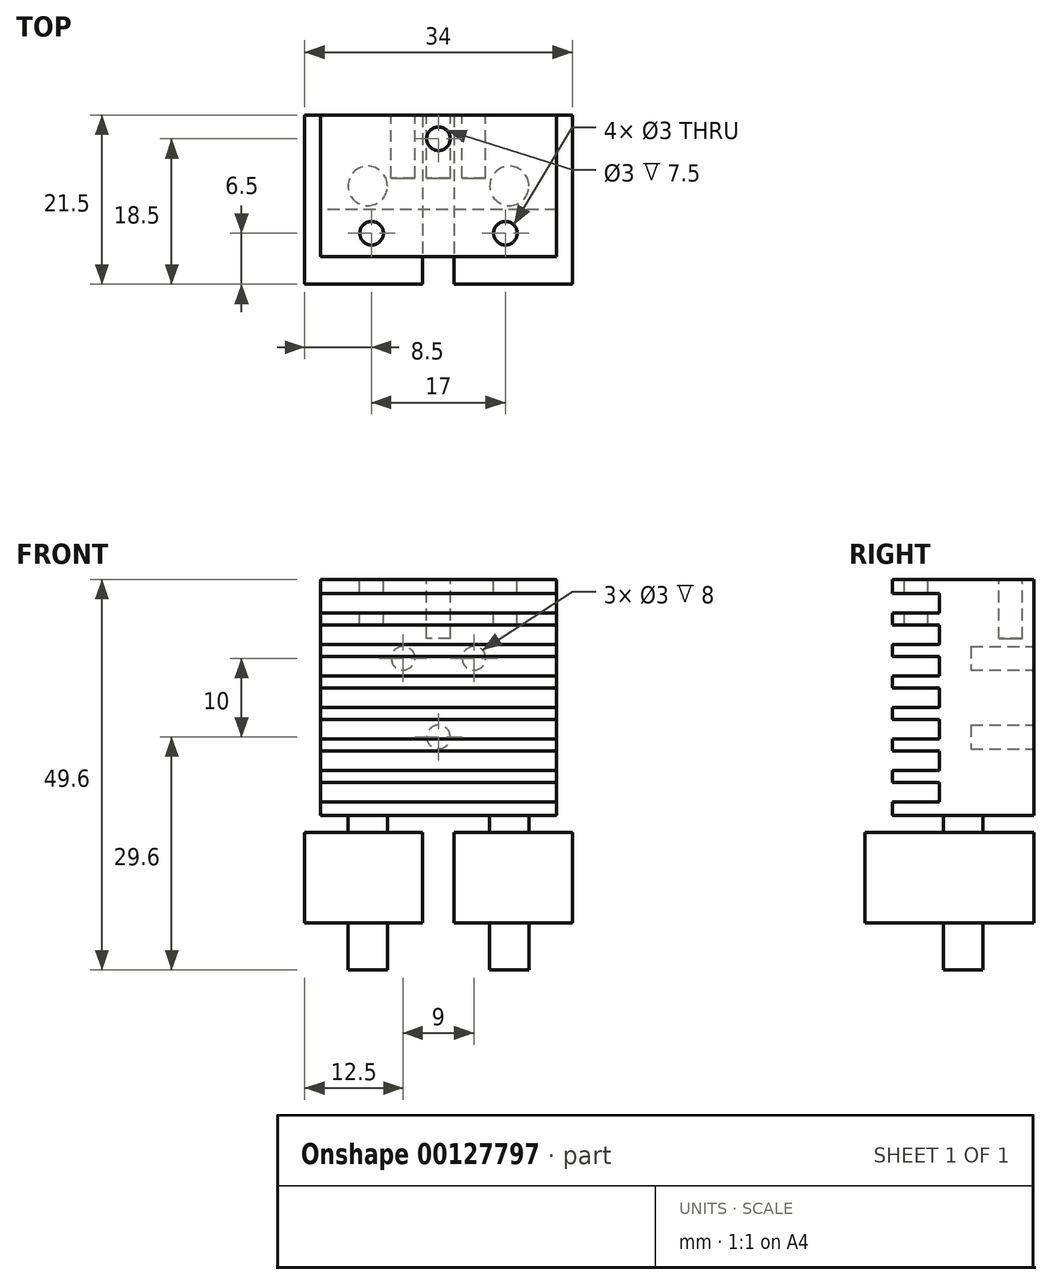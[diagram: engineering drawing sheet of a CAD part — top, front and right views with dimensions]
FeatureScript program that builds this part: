
annotation { "Feature Type Name" : "Feature", "Feature Type Description" : "" }
export const myFeature = defineFeature(function(context is Context, id is Id, definition is map)
    precondition{}
    {
        {
            var Q0;
            Q0=qCreatedBy(makeId("Front.planeOp"),FACE);
            var sketch = newSketch(context, id + "F0", { "sketchPlane" : qUnion([Q0])});
            skLineSegment(sketch, "E0.bottom", {"start": v(15, 15) * mm, "end": v(-15, 15) * mm});
            skLineSegment(sketch, "E0.top", {"start": v(15, -15) * mm, "end": v(-15, -15) * mm});
            skLineSegment(sketch, "E0.left", {"start": v(15, 15) * mm, "end": v(15, -15) * mm});
            skLineSegment(sketch, "E0.right", {"start": v(-15, 15) * mm, "end": v(-15, -15) * mm});
            skPoint(sketch, "E0.middle", {"position": v(0, 0) * mm});
            skSolve(sketch);
        }
        {
            var Q0;
            Q0 = qSketchRegion(id + "F0", true);
            extrude(context, id + "F1", {"entities" : qUnion([Q0]), "endBound" : BoundingType.SYMMETRIC, "depth" : 18 * mm});
        }
        {
            var Q0;
            Q0=makeQuery(id+"F1.opExtrude","SWEPT_FACE",FACE,{"disambiguationData":[OSD([sQuery(id+"F0.wireOp",EDGE,"E0.top")])]});
            var sketch = newSketch(context, id + "F2", { "sketchPlane" : qUnion([Q0])});
            skCircle(sketch, "E1", {"center": v(-9, 0) * mm, "radius": 2.5 * mm});
            skLineSegment(sketch, "E2", {"start": v(0, 0) * mm, "end": v(0, 26.39) * mm, "construction": true});
            skPoint(sketch, "E2.endSnap0", {"position": v(0, 9) * mm});
            skCircle(sketch, "E3.MirrorC", {"center": v(9, 0) * mm, "radius": 2.5 * mm});
            skSolve(sketch);
        }
        {
            var Q0;
            Q0 = qSketchRegion(id + "F2", true);
            extrude(context, id + "F3", {"entities" : qUnion([Q0]), "operationType" : NewBodyOperationType.ADD, "depth" : (49.6 - 30) * mm});
        }
        {
            var Q0;
            Q0=makeQuery(id+"F1.opExtrude","SWEPT_FACE",FACE,{"disambiguationData":[OSD([sQuery(id+"F0.wireOp",EDGE,"E0.right")])]});
            var sketch = newSketch(context, id + "F4", { "sketchPlane" : qUnion([Q0])});
            skLineSegment(sketch, "E4.bottom", {"start": v(9, 13.25) * mm, "end": v(3, 13.25) * mm});
            skLineSegment(sketch, "E4.top", {"start": v(9, 10.75) * mm, "end": v(3, 10.75) * mm});
            skLineSegment(sketch, "E4.left", {"start": v(9, 13.25) * mm, "end": v(9, 10.75) * mm});
            skLineSegment(sketch, "E4.right", {"start": v(3, 13.25) * mm, "end": v(3, 10.75) * mm});
            skLineSegment(sketch, "E5.1.0.0", {"start": v(3, 9.25) * mm, "end": v(3, 6.75) * mm});
            skLineSegment(sketch, "E5.1.0.1", {"start": v(9, 9.25) * mm, "end": v(9, 6.75) * mm});
            skLineSegment(sketch, "E5.1.0.2", {"start": v(9, 6.75) * mm, "end": v(3, 6.75) * mm});
            skLineSegment(sketch, "E5.1.0.3", {"start": v(9, 9.25) * mm, "end": v(3, 9.25) * mm});
            skLineSegment(sketch, "E5.2.0.0", {"start": v(3, 5.25) * mm, "end": v(3, 2.75) * mm});
            skLineSegment(sketch, "E5.2.0.1", {"start": v(9, 5.25) * mm, "end": v(9, 2.75) * mm});
            skLineSegment(sketch, "E5.2.0.2", {"start": v(9, 2.75) * mm, "end": v(3, 2.75) * mm});
            skLineSegment(sketch, "E5.2.0.3", {"start": v(9, 5.25) * mm, "end": v(3, 5.25) * mm});
            skLineSegment(sketch, "E5.direction1", {"start": v(3, 10.75) * mm, "end": v(3, 6.75) * mm, "construction": true});
            skLineSegment(sketch, "E6.0.3.0", {"start": v(3, 1.25) * mm, "end": v(3, -1.25) * mm});
            skLineSegment(sketch, "E6.3.3.0", {"start": v(9, 1.25) * mm, "end": v(9, -1.25) * mm});
            skLineSegment(sketch, "E6.6.3.0", {"start": v(9, -1.25) * mm, "end": v(3, -1.25) * mm});
            skLineSegment(sketch, "E6.9.3.0", {"start": v(9, 1.25) * mm, "end": v(3, 1.25) * mm});
            skLineSegment(sketch, "E6.0.4.0", {"start": v(3, -2.75) * mm, "end": v(3, -5.25) * mm});
            skLineSegment(sketch, "E6.3.4.0", {"start": v(9, -2.75) * mm, "end": v(9, -5.25) * mm});
            skLineSegment(sketch, "E6.6.4.0", {"start": v(9, -5.25) * mm, "end": v(3, -5.25) * mm});
            skLineSegment(sketch, "E6.9.4.0", {"start": v(9, -2.75) * mm, "end": v(3, -2.75) * mm});
            skLineSegment(sketch, "E7.0.5.0", {"start": v(3, -6.75) * mm, "end": v(3, -9.25) * mm});
            skLineSegment(sketch, "E7.3.5.0", {"start": v(9, -6.75) * mm, "end": v(9, -9.25) * mm});
            skLineSegment(sketch, "E7.6.5.0", {"start": v(9, -9.25) * mm, "end": v(3, -9.25) * mm});
            skLineSegment(sketch, "E7.9.5.0", {"start": v(9, -6.75) * mm, "end": v(3, -6.75) * mm});
            skLineSegment(sketch, "E8.0.6.0", {"start": v(3, -10.75) * mm, "end": v(3, -13.25) * mm});
            skLineSegment(sketch, "E8.3.6.0", {"start": v(9, -10.75) * mm, "end": v(9, -13.25) * mm});
            skLineSegment(sketch, "E8.6.6.0", {"start": v(9, -13.25) * mm, "end": v(3, -13.25) * mm});
            skLineSegment(sketch, "E8.9.6.0", {"start": v(9, -10.75) * mm, "end": v(3, -10.75) * mm});
            skSolve(sketch);
        }
        {
            var Q0;
            Q0 = qSketchRegion(id + "F4", true);
            extrude(context, id + "F5", {"entities" : qUnion([Q0]), "operationType" : NewBodyOperationType.REMOVE, "endBound" : BoundingType.THROUGH_ALL, "oppositeDirection" : true, "depth" : 25 * mm});
        }
        {
            var Q0;
            Q0=makeQuery(id+"F1.opExtrude","CAP_FACE",FACE,{"disambiguationData":[OSD([sQuery(id+"F0.wireOp",EDGE,"E0.bottom"),sQuery(id+"F0.wireOp",EDGE,"E0.top"),sQuery(id+"F0.wireOp",EDGE,"E0.left"),sQuery(id+"F0.wireOp",EDGE,"E0.right")])],"isStart":true});
            var sketch = newSketch(context, id + "F6", { "sketchPlane" : qUnion([Q0])});
            skCircle(sketch, "E9", {"center": v(0, -5) * mm, "radius": 1.5 * mm});
            skCircle(sketch, "E10", {"center": v(-4.5, 5) * mm, "radius": 1.5 * mm});
            skCircle(sketch, "E11", {"center": v(4.5, 5) * mm, "radius": 1.5 * mm});
            skLineSegment(sketch, "E12", {"start": v(0, 0) * mm, "end": v(0, 11.94) * mm, "construction": true});
            skSolve(sketch);
        }
        {
            var Q0;
            Q0 = qSketchRegion(id + "F6", true);
            extrude(context, id + "F7", {"entities" : qUnion([Q0]), "operationType" : NewBodyOperationType.REMOVE, "oppositeDirection" : true, "depth" : 8 * mm});
        }
        {
            var Q0;
            Q0=makeQuery(id+"F1.opExtrude","SWEPT_FACE",FACE,{"disambiguationData":[OSD([sQuery(id+"F0.wireOp",EDGE,"E0.bottom")])]});
            var sketch = newSketch(context, id + "F8", { "sketchPlane" : qUnion([Q0])});
            skCircle(sketch, "E13", {"center": v(0, 6) * mm, "radius": 1.5 * mm});
            skCircle(sketch, "E14", {"center": v(8.5, -6) * mm, "radius": 1.5 * mm});
            skCircle(sketch, "E15", {"center": v(-8.5, -6) * mm, "radius": 1.5 * mm});
            skLineSegment(sketch, "E16", {"start": v(0, 0) * mm, "end": v(0, -17.41) * mm, "construction": true});
            skSolve(sketch);
        }
        {
            var Q0;
            Q0 = qSketchRegion(id + "F8", true);
            extrude(context, id + "F9", {"entities" : qUnion([Q0]), "operationType" : NewBodyOperationType.REMOVE, "oppositeDirection" : true, "depth" : 7.5 * mm});
        }
        {
            var Q0;
            Q0=makeQuery(id+"F1.opExtrude","SWEPT_FACE",FACE,{"disambiguationData":[OSD([sQuery(id+"F0.wireOp",EDGE,"E0.top")])]});
            cPlane(context, id + "F10", {"entities" : qUnion([Q0]), "cplaneType" : CPlaneType.OFFSET, "offset" : 2.1 * mm, "width" : 150 * mm, "height" : 150 * mm});
        }
        {
            var Q0;
            Q0=qCreatedBy(id+"F10.planeOp",FACE);
            var sketch = newSketch(context, id + "F11", { "sketchPlane" : qUnion([Q0])});
            skLineSegment(sketch, "E17.bottom", {"start": v(-17, -9) * mm, "end": v(-2, -9) * mm});
            skLineSegment(sketch, "E17.top", {"start": v(-17, 12.5) * mm, "end": v(-2, 12.5) * mm});
            skLineSegment(sketch, "E17.left", {"start": v(-17, -9) * mm, "end": v(-17, 12.5) * mm});
            skLineSegment(sketch, "E17.right", {"start": v(-2, -9) * mm, "end": v(-2, 12.5) * mm});
            skLineSegment(sketch, "E18", {"start": v(0, 0) * mm, "end": v(0, -21.53) * mm, "construction": true});
            skLineSegment(sketch, "E19.MirrorCS", {"start": v(2, -9) * mm, "end": v(2, 12.5) * mm});
            skLineSegment(sketch, "E20.MirrorCS", {"start": v(17, -9) * mm, "end": v(17, 12.5) * mm});
            skLineSegment(sketch, "E21.MirrorCS", {"start": v(17, -9) * mm, "end": v(2, -9) * mm});
            skLineSegment(sketch, "E22.MirrorCS", {"start": v(17, 12.5) * mm, "end": v(2, 12.5) * mm});
            skSolve(sketch);
        }
        {
            var Q0;
            Q0 = qSketchRegion(id + "F11", true);
            extrude(context, id + "F12", {"entities" : qUnion([Q0]), "operationType" : NewBodyOperationType.ADD, "depth" : (43.6 - 32.1) * mm});
        }
    });
